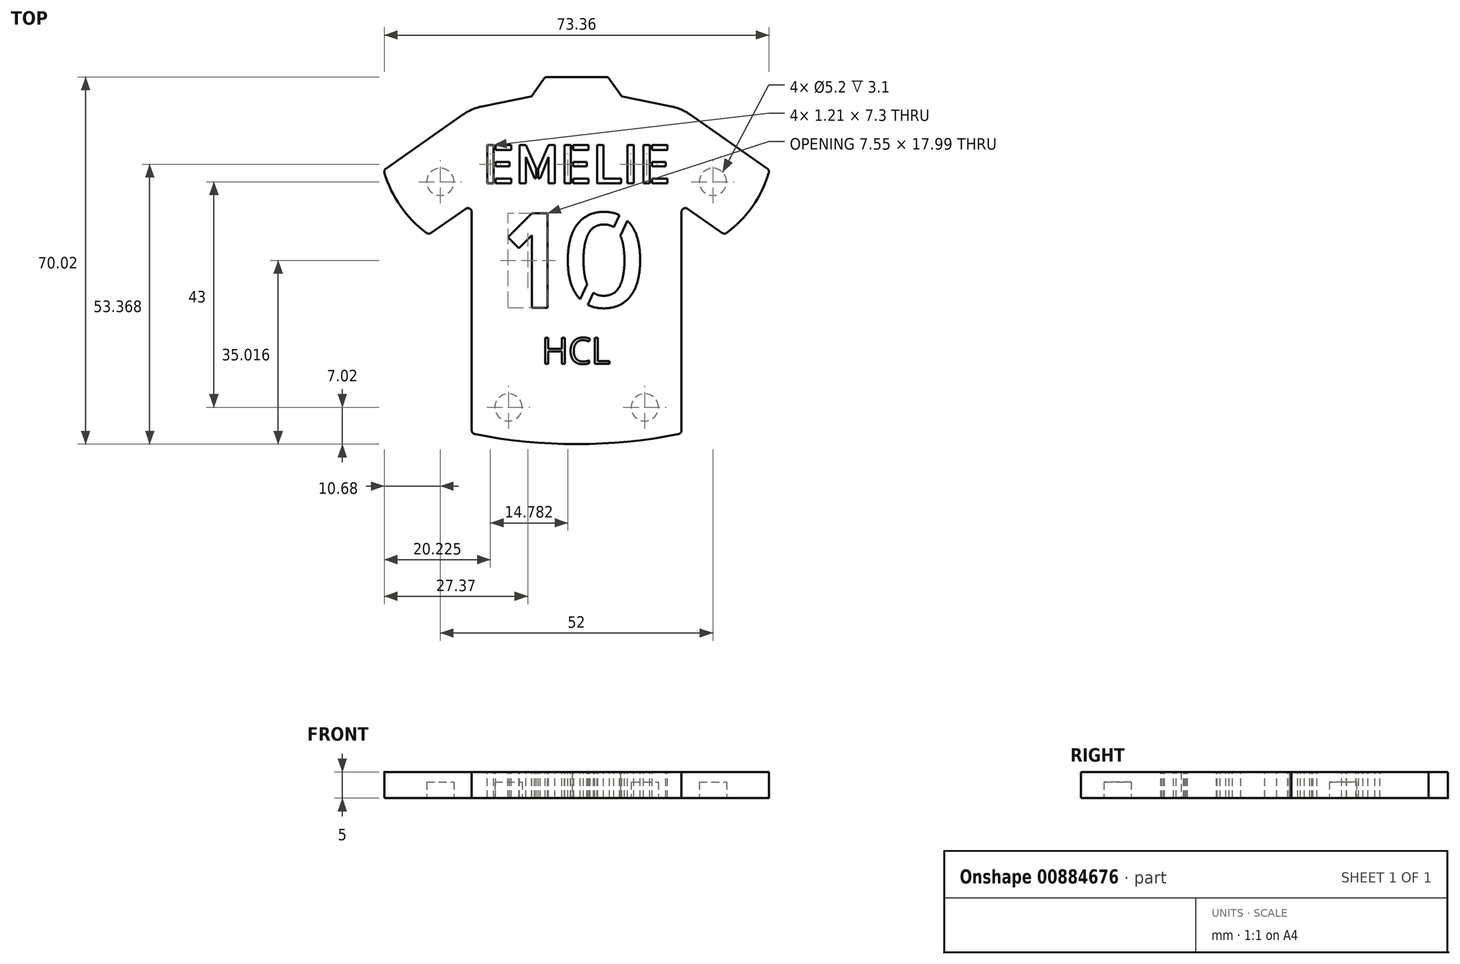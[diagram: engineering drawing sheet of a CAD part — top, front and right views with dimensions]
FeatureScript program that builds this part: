
annotation { "Feature Type Name" : "Feature", "Feature Type Description" : "" }
export const myFeature = defineFeature(function(context is Context, id is Id, definition is map)
    precondition{}
    {
        {
            var Q0;
            Q0=qCreatedBy(makeId("Top.planeOp"),FACE);
            var sketch = newSketch(context, id + "F0", { "sketchPlane" : qUnion([Q0])});
            skLineSegment(sketch, "E0", {"start": v(0, 0) * mm, "end": v(0, -62) * mm, "construction": true});
            skLineSegment(sketch, "E1", {"start": v(0, -62) * mm, "end": v(-20, -62) * mm, "construction": true});
            skLineSegment(sketch, "E2", {"start": v(-20, -62) * mm, "end": v(-20, -18.31) * mm});
            skLineSegment(sketch, "E3", {"start": v(-20, -18.31) * mm, "end": v(-28.2, -24.05) * mm});
            skLineSegment(sketch, "E4", {"start": v(-28.2, -24.05) * mm, "end": v(-36.8, -11.76) * mm, "construction": true});
            skLineSegment(sketch, "E5", {"start": v(-36.8, -11.76) * mm, "end": v(-20, 0) * mm});
            skLineSegment(sketch, "E6.MirrorCS", {"start": v(36.8, -11.76) * mm, "end": v(20, 0) * mm});
            skLineSegment(sketch, "E7.MirrorCS", {"start": v(28.2, -24.05) * mm, "end": v(36.8, -11.76) * mm, "construction": true});
            skLineSegment(sketch, "E8.MirrorCS", {"start": v(20, -62) * mm, "end": v(20, -18.31) * mm});
            skLineSegment(sketch, "E9.MirrorCS", {"start": v(0, -62) * mm, "end": v(20, -62) * mm, "construction": true});
            skLineSegment(sketch, "E10.MirrorCS", {"start": v(20, -18.31) * mm, "end": v(28.2, -24.05) * mm});
            skPoint(sketch, "E11.orphan", {"position": v(0, 0) * mm});
            skLineSegment(sketch, "E12", {"start": v(-20, 0) * mm, "end": v(0, 4) * mm});
            skLineSegment(sketch, "E13", {"start": v(20, 0) * mm, "end": v(0, 4) * mm});
            skArc(sketch, "E14", {"start": v(-36.8, -11.76) * mm, "mid": v(-33.57, -18.66) * mm, "end": v(-28.2, -24.05) * mm});
            skArc(sketch, "E15", {"start": v(28.2, -24.05) * mm, "mid": v(33.57, -18.66) * mm, "end": v(36.8, -11.76) * mm});
            skArc(sketch, "E16", {"start": v(-20, -62) * mm, "mid": v(0, -64.02) * mm, "end": v(20, -62) * mm});
            skSolve(sketch);
        }
        {
            var Q0;
            Q0 = qSketchRegion(id + "F0", true);
            extrude(context, id + "F1", {"entities" : qUnion([Q0]), "depth" : 5 * mm, "offsetDistance" : 25 * mm});
        }
        {
            var Q0;
            Q0=makeQuery(id+"F1.opExtrude","CAP_FACE",FACE,{"disambiguationData":[OSD([sQuery(id+"F0.wireOp",EDGE,"E1"),sQuery(id+"F0.wireOp",EDGE,"E2"),sQuery(id+"F0.wireOp",EDGE,"E3"),sQuery(id+"F0.wireOp",EDGE,"E4"),sQuery(id+"F0.wireOp",EDGE,"E5"),sQuery(id+"F0.wireOp",EDGE,"IlW5oEZI-P582-iyz9-SPjp-bK7lNdtFADA4"),sQuery(id+"F0.wireOp",EDGE,"b0af1ca9-168d-4077-b48c-e6805785c7b00.MirrorCS"),sQuery(id+"F0.wireOp",EDGE,"E6.MirrorCS"),sQuery(id+"F0.wireOp",EDGE,"E7.MirrorCS"),sQuery(id+"F0.wireOp",EDGE,"E8.MirrorCS"),sQuery(id+"F0.wireOp",EDGE,"E9.MirrorCS"),sQuery(id+"F0.wireOp",EDGE,"E10.MirrorCS")])],"isStart":true});
            var Q1;
            Q1=makeQuery(id+"F1.opExtrude","CAP_FACE",FACE,{"disambiguationData":[OSD([sQuery(id+"F0.wireOp",EDGE,"E1"),sQuery(id+"F0.wireOp",EDGE,"E2"),sQuery(id+"F0.wireOp",EDGE,"E3"),sQuery(id+"F0.wireOp",EDGE,"E4"),sQuery(id+"F0.wireOp",EDGE,"E5"),sQuery(id+"F0.wireOp",EDGE,"E6.MirrorCS"),sQuery(id+"F0.wireOp",EDGE,"E7.MirrorCS"),sQuery(id+"F0.wireOp",EDGE,"E8.MirrorCS"),sQuery(id+"F0.wireOp",EDGE,"E9.MirrorCS"),sQuery(id+"F0.wireOp",EDGE,"E10.MirrorCS"),sQuery(id+"F0.wireOp",EDGE,"E12"),sQuery(id+"F0.wireOp",EDGE,"E13")])],"isStart":false});
            var sketch = newSketch(context, id + "F2", { "sketchPlane" : qUnion([Q0, Q1])});
            skCircle(sketch, "E17", {"center": v(13, 57) * mm, "radius": 2.6 * mm});
            skCircle(sketch, "E18", {"center": v(-13, 57) * mm, "radius": 2.6 * mm});
            skCircle(sketch, "E19", {"center": v(26, 14) * mm, "radius": 2.6 * mm});
            skCircle(sketch, "E20", {"center": v(-26, 14) * mm, "radius": 2.6 * mm});
            skSolve(sketch);
        }
        {
            var Q0;
            Q0 = qSketchRegion(id + "F2", true);
            extrude(context, id + "F3", {"entities" : qUnion([Q0]), "operationType" : NewBodyOperationType.REMOVE, "oppositeDirection" : true, "depth" : 3.1 * mm, "offsetDistance" : 25 * mm});
        }
        {
            var Q0;
            Q0=makeQuery(id+"F1.opExtrude","CAP_FACE",FACE,{"disambiguationData":[OSD([sQuery(id+"F0.wireOp",EDGE,"E1"),sQuery(id+"F0.wireOp",EDGE,"E2"),sQuery(id+"F0.wireOp",EDGE,"E3"),sQuery(id+"F0.wireOp",EDGE,"E4"),sQuery(id+"F0.wireOp",EDGE,"E5"),sQuery(id+"F0.wireOp",EDGE,"IlW5oEZI-P582-iyz9-SPjp-bK7lNdtFADA4"),sQuery(id+"F0.wireOp",EDGE,"b0af1ca9-168d-4077-b48c-e6805785c7b00.MirrorCS"),sQuery(id+"F0.wireOp",EDGE,"E6.MirrorCS"),sQuery(id+"F0.wireOp",EDGE,"E7.MirrorCS"),sQuery(id+"F0.wireOp",EDGE,"E8.MirrorCS"),sQuery(id+"F0.wireOp",EDGE,"E9.MirrorCS"),sQuery(id+"F0.wireOp",EDGE,"E10.MirrorCS"),sQuery(id+"F0.wireOp",EDGE,"k2Sst70w-Y1rZ-SRoK-z35Y-7HSdN3ftnpVl")])],"isStart":false});
            var sketch = newSketch(context, id + "F4", { "sketchPlane" : qUnion([Q0])});
            skText(sketch, "E21", { "text": "EMELIE", "fontName": "AllertaStencil-Regular.ttf"});
            skText(sketch, "E22", { "text": "10", "fontName": "AllertaStencil-Regular.ttf"});
            skText(sketch, "E23", { "text": "HCL", "fontName": "OpenSans-Regular.ttf"});
            const initialGuessF4  = {"E21": [-0.018, -0.0143, 1, 0, 0.0073], "E22": [-0.01379, -0.038, 1, 0, 0.018], "E23": [-0.0067, -0.0487, 1, 0, 0.005]};
            skSetInitialGuess(sketch, initialGuessF4);
            skSolve(sketch);
        }
        {
            var Q0;
            Q0 = qSketchRegion(id + "F4", true);
            extrude(context, id + "F5", {"entities" : qUnion([Q0]), "operationType" : NewBodyOperationType.REMOVE, "endBound" : BoundingType.THROUGH_ALL, "oppositeDirection" : true, "depth" : 25 * mm, "offsetDistance" : 25 * mm});
        }
        {
            var Q0;
            Q0=makeQuery(id+"F1.opExtrude","CAP_FACE",FACE,{"disambiguationData":[OSD([sQuery(id+"F0.wireOp",EDGE,"E1"),sQuery(id+"F0.wireOp",EDGE,"E2"),sQuery(id+"F0.wireOp",EDGE,"E3"),sQuery(id+"F0.wireOp",EDGE,"E4"),sQuery(id+"F0.wireOp",EDGE,"E5"),sQuery(id+"F0.wireOp",EDGE,"E6.MirrorCS"),sQuery(id+"F0.wireOp",EDGE,"E7.MirrorCS"),sQuery(id+"F0.wireOp",EDGE,"E8.MirrorCS"),sQuery(id+"F0.wireOp",EDGE,"E9.MirrorCS"),sQuery(id+"F0.wireOp",EDGE,"E10.MirrorCS"),sQuery(id+"F0.wireOp",EDGE,"E12"),sQuery(id+"F0.wireOp",EDGE,"E13")])],"isStart":false});
            var sketch = newSketch(context, id + "F6", { "sketchPlane" : qUnion([Q0])});
            skLineSegment(sketch, "E24", {"start": v(-8.6, 2.28) * mm, "end": v(-6, 6) * mm});
            skLineSegment(sketch, "E25", {"start": v(-6, 6) * mm, "end": v(6, 6) * mm});
            skLineSegment(sketch, "E26", {"start": v(6, 6) * mm, "end": v(8.6, 2.28) * mm});
            skLineSegment(sketch, "E27", {"start": v(-8.6, 2.28) * mm, "end": v(0, 4) * mm});
            skLineSegment(sketch, "E28", {"start": v(0, 4) * mm, "end": v(8.6, 2.28) * mm});
            skSolve(sketch);
        }
        {
            var Q0;
            Q0 = qSketchRegion(id + "F6", true);
            extrude(context, id + "F7", {"entities" : qUnion([Q0]), "operationType" : NewBodyOperationType.ADD, "oppositeDirection" : true, "depth" : 5 * mm, "offsetDistance" : 25 * mm});
        }
        {
            var Q0;
            Q0=makeQuery(id+"F1.opExtrude","SWEPT_EDGE",EDGE,{"disambiguationData":[OSD([sQuery(id+"F0.wireOp",EDGE,"E5"),sQuery(id+"F0.wireOp",EDGE,"E12")])]});
            var Q1;
            Q1=makeQuery(id+"F1.opExtrude","SWEPT_EDGE",EDGE,{"disambiguationData":[OSD([sQuery(id+"F0.wireOp",EDGE,"E6.MirrorCS"),sQuery(id+"F0.wireOp",EDGE,"E13")])]});
            fillet(context, id + "F8", {"entities" : qUnion([Q0, Q1]), "radius" : 10 * mm, "tangentPropagation" : true, "allowEdgeOverflow" : false});
        }
        {
            var Q0;
            Q0=makeQuery(id+"F7.opExtrude","SWEPT_EDGE",EDGE,{"disambiguationData":[OSD([sQuery(id+"F6.wireOp",EDGE,"E24"),sQuery(id+"F6.wireOp",EDGE,"E25")])]});
            var Q1;
            Q1=makeQuery(id+"F7.opExtrude","SWEPT_EDGE",EDGE,{"disambiguationData":[OSD([sQuery(id+"F6.wireOp",EDGE,"E25"),sQuery(id+"F6.wireOp",EDGE,"E26")])]});
            var Q2;
            Q2=makeQuery(id+"F7.opExtrude","SWEPT_EDGE",EDGE,{"disambiguationData":[OSD([sQuery(id+"F0.wireOp",EDGE,"E12"),sQuery(id+"F6.wireOp",EDGE,"E24"),sQuery(id+"F6.wireOp",EDGE,"E27")])]});
            var Q3;
            Q3=makeQuery(id+"F1.opExtrude","SWEPT_EDGE",EDGE,{"disambiguationData":[OSD([sQuery(id+"F0.wireOp",EDGE,"E5"),sQuery(id+"F0.wireOp",EDGE,"E14")])]});
            var Q4;
            Q4=makeQuery(id+"F1.opExtrude","SWEPT_EDGE",EDGE,{"disambiguationData":[OSD([sQuery(id+"F0.wireOp",EDGE,"E6.MirrorCS"),sQuery(id+"F0.wireOp",EDGE,"E15")])]});
            var Q5;
            Q5=makeQuery(id+"F1.opExtrude","SWEPT_EDGE",EDGE,{"disambiguationData":[OSD([sQuery(id+"F0.wireOp",EDGE,"E10.MirrorCS"),sQuery(id+"F0.wireOp",EDGE,"E15")])]});
            var Q6;
            Q6=makeQuery(id+"F1.opExtrude","SWEPT_EDGE",EDGE,{"disambiguationData":[OSD([sQuery(id+"F0.wireOp",EDGE,"E8.MirrorCS"),sQuery(id+"F0.wireOp",EDGE,"E10.MirrorCS")])]});
            var Q7;
            Q7=makeQuery(id+"F1.opExtrude","SWEPT_EDGE",EDGE,{"disambiguationData":[OSD([sQuery(id+"F0.wireOp",EDGE,"E2"),sQuery(id+"F0.wireOp",EDGE,"E3")])]});
            var Q8;
            Q8=makeQuery(id+"F1.opExtrude","SWEPT_EDGE",EDGE,{"disambiguationData":[OSD([sQuery(id+"F0.wireOp",EDGE,"E2"),sQuery(id+"F0.wireOp",EDGE,"E16")])]});
            var Q9;
            Q9=makeQuery(id+"F1.opExtrude","SWEPT_EDGE",EDGE,{"disambiguationData":[OSD([sQuery(id+"F0.wireOp",EDGE,"E8.MirrorCS"),sQuery(id+"F0.wireOp",EDGE,"E16")])]});
            var Q10;
            Q10=makeQuery(id+"F1.opExtrude","SWEPT_EDGE",EDGE,{"disambiguationData":[OSD([sQuery(id+"F0.wireOp",EDGE,"E3"),sQuery(id+"F0.wireOp",EDGE,"E14")])]});
            var Q11;
            Q11=makeQuery(id+"F7.opExtrude","SWEPT_EDGE",EDGE,{"disambiguationData":[OSD([sQuery(id+"F0.wireOp",EDGE,"E13"),sQuery(id+"F6.wireOp",EDGE,"E26"),sQuery(id+"F6.wireOp",EDGE,"E28")])]});
            fillet(context, id + "F9", {"entities" : qUnion([Q0, Q1, Q2, Q3, Q4, Q5, Q6, Q7, Q8, Q9, Q10, Q11]), "radius" : 0.75 * mm, "tangentPropagation" : true, "allowEdgeOverflow" : false});
        }
    });
